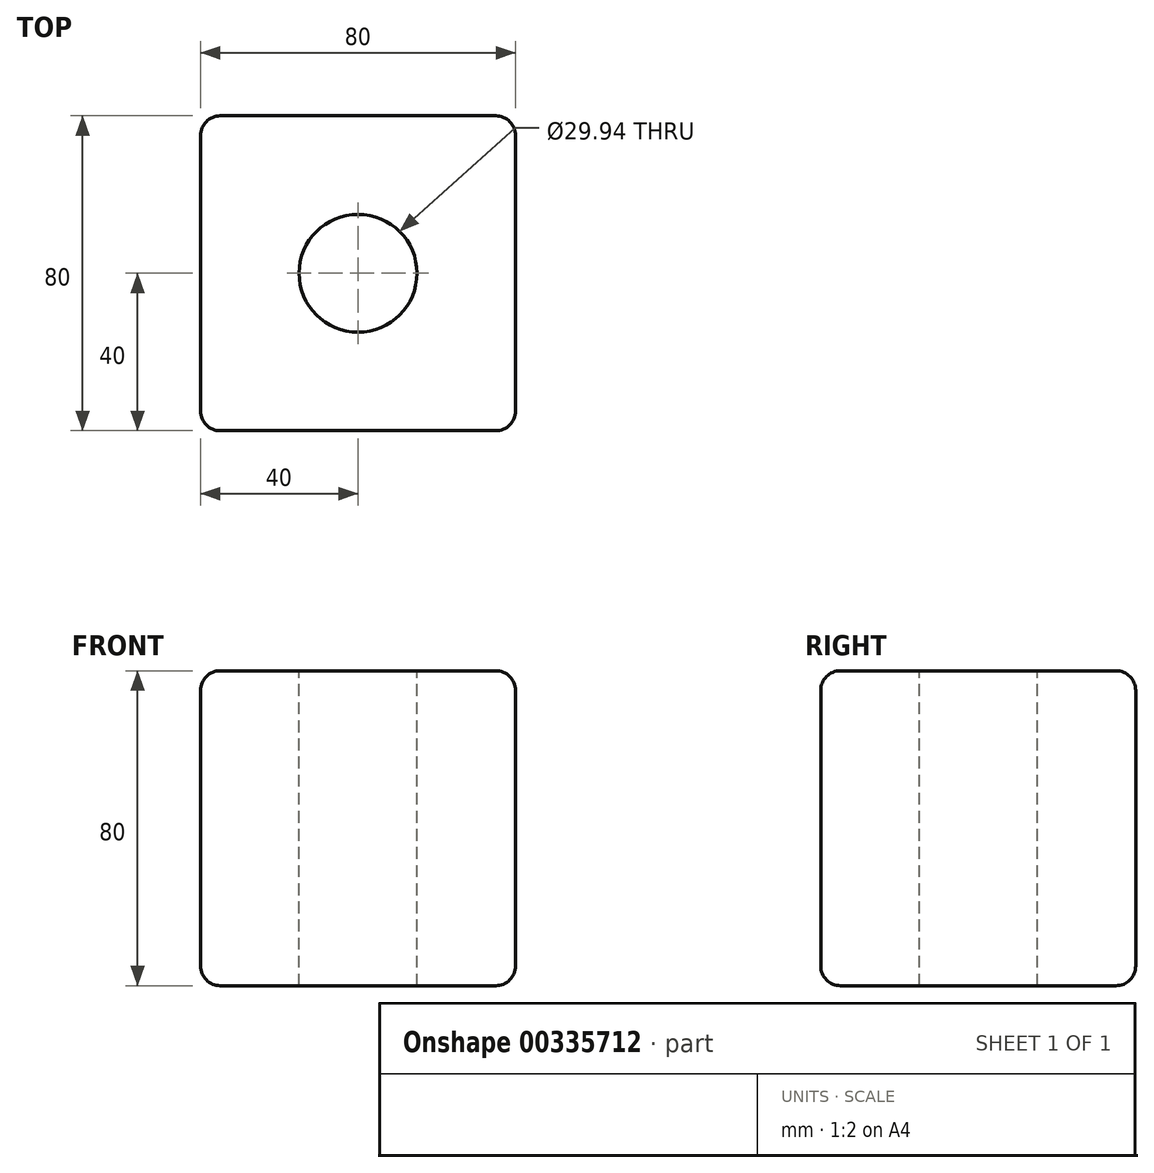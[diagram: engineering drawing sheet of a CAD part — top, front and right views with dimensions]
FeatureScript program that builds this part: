
annotation { "Feature Type Name" : "Feature", "Feature Type Description" : "" }
export const myFeature = defineFeature(function(context is Context, id is Id, definition is map)
    precondition{}
    {
        {
            var Q0;
            Q0=qCreatedBy(makeId("Top.planeOp"),FACE);
            var sketch = newSketch(context, id + "F0", { "sketchPlane" : qUnion([Q0])});
            skLineSegment(sketch, "E0.bottom", {"start": v(-40, 40) * mm, "end": v(40, 40) * mm});
            skLineSegment(sketch, "E0.top", {"start": v(-40, -40) * mm, "end": v(40, -40) * mm});
            skLineSegment(sketch, "E0.left", {"start": v(-40, 40) * mm, "end": v(-40, -40) * mm});
            skLineSegment(sketch, "E0.right", {"start": v(40, 40) * mm, "end": v(40, -40) * mm});
            skPoint(sketch, "E0.middle", {"position": v(0, 0) * mm});
            skSolve(sketch);
        }
        {
            var Q0;
            Q0=makeQuery(id+"F0.imprint","IMPRINT",FACE,{"disambiguationData":[TD([[makeQuery(id+"F0.imprint","IMPRINT",EDGE,{"derivedFrom":sQuery(id+"F0.wireOp",EDGE,"E0.bottom")}),-1.0]])]});
            extrude(context, id + "F1", {"entities" : qUnion([Q0]), "endBound" : BoundingType.SYMMETRIC, "depth" : 80 * mm});
        }
        {
            var Q0;
            Q0=makeQuery(id+"F1.opExtrude","CAP_EDGE",EDGE,{"disambiguationData":[OSD([sQuery(id+"F0.wireOp",EDGE,"E0.top")])],"isStart":false});
            var Q1;
            Q1=makeQuery(id+"F1.opExtrude","SWEPT_EDGE",EDGE,{"disambiguationData":[OSD([sQuery(id+"F0.wireOp",EDGE,"E0.top"),sQuery(id+"F0.wireOp",EDGE,"E0.right")])]});
            var Q2;
            Q2=makeQuery(id+"F1.opExtrude","CAP_EDGE",EDGE,{"disambiguationData":[OSD([sQuery(id+"F0.wireOp",EDGE,"E0.top")])],"isStart":true});
            var Q3;
            Q3=makeQuery(id+"F1.opExtrude","SWEPT_EDGE",EDGE,{"disambiguationData":[OSD([sQuery(id+"F0.wireOp",EDGE,"E0.top"),sQuery(id+"F0.wireOp",EDGE,"E0.left")])]});
            var Q4;
            Q4=makeQuery(id+"F1.opExtrude","CAP_EDGE",EDGE,{"disambiguationData":[OSD([sQuery(id+"F0.wireOp",EDGE,"E0.left")])],"isStart":false});
            var Q5;
            Q5=makeQuery(id+"F1.opExtrude","CAP_EDGE",EDGE,{"disambiguationData":[OSD([sQuery(id+"F0.wireOp",EDGE,"E0.left")])],"isStart":true});
            var Q6;
            Q6=makeQuery(id+"F1.opExtrude","SWEPT_EDGE",EDGE,{"disambiguationData":[OSD([sQuery(id+"F0.wireOp",EDGE,"E0.bottom"),sQuery(id+"F0.wireOp",EDGE,"E0.left")])]});
            var Q7;
            Q7=makeQuery(id+"F1.opExtrude","CAP_EDGE",EDGE,{"disambiguationData":[OSD([sQuery(id+"F0.wireOp",EDGE,"E0.right")])],"isStart":false});
            var Q8;
            Q8=makeQuery(id+"F1.opExtrude","CAP_EDGE",EDGE,{"disambiguationData":[OSD([sQuery(id+"F0.wireOp",EDGE,"E0.bottom")])],"isStart":false});
            var Q9;
            Q9=makeQuery(id+"F1.opExtrude","CAP_EDGE",EDGE,{"disambiguationData":[OSD([sQuery(id+"F0.wireOp",EDGE,"E0.bottom")])],"isStart":true});
            var Q10;
            Q10=makeQuery(id+"F1.opExtrude","CAP_EDGE",EDGE,{"disambiguationData":[OSD([sQuery(id+"F0.wireOp",EDGE,"E0.right")])],"isStart":true});
            var Q11;
            Q11=makeQuery(id+"F1.opExtrude","SWEPT_EDGE",EDGE,{"disambiguationData":[OSD([sQuery(id+"F0.wireOp",EDGE,"E0.bottom"),sQuery(id+"F0.wireOp",EDGE,"E0.right")])]});
            fillet(context, id + "F2", {"entities" : qUnion([Q0, Q1, Q2, Q3, Q4, Q5, Q6, Q7, Q8, Q9, Q10, Q11]), "radius" : 5 * mm, "tangentPropagation" : true, "allowEdgeOverflow" : false});
        }
        {
            var Q0;
            Q0=makeQuery(id+"F1.opExtrude","CAP_FACE",FACE,{"disambiguationData":[OSD([sQuery(id+"F0.wireOp",EDGE,"E0.bottom"),sQuery(id+"F0.wireOp",EDGE,"E0.top"),sQuery(id+"F0.wireOp",EDGE,"E0.left"),sQuery(id+"F0.wireOp",EDGE,"E0.right")])],"isStart":false});
            var sketch = newSketch(context, id + "F3", { "sketchPlane" : qUnion([Q0])});
            skCircle(sketch, "E1", {"center": v(0, 0) * mm, "radius": 14.97 * mm});
            skSolve(sketch);
        }
        {
            var Q0;
            Q0 = qSketchRegion(id + "F3", true);
            extrude(context, id + "F4", {"entities" : qUnion([Q0]), "operationType" : NewBodyOperationType.REMOVE, "endBound" : BoundingType.THROUGH_ALL, "oppositeDirection" : true, "depth" : 25 * mm});
        }
    });
